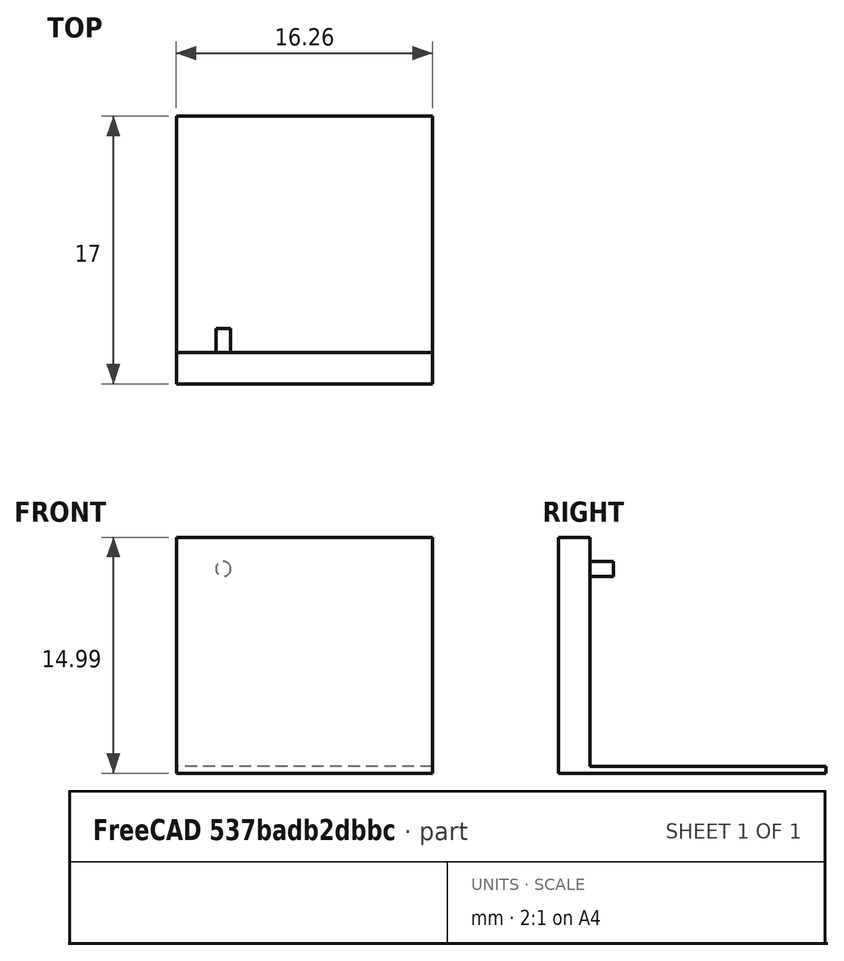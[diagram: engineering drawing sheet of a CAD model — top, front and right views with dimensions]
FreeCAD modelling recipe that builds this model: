
FCSTD DOCUMENT  (FreeCAD 0.20R29603 (Git))
Label: base
License: All rights reserved
LicenseURL: http://en.wikipedia.org/wiki/All_rights_reserved
objects: Mesh::Feature×5, Sketcher::SketchObject×3, PartDesign::Pad×3, PartDesign::Plane×1, PartDesign::Line×1, PartDesign::Point×1, PartDesign::Body×1
note: 13 computed .brp shape members not serialized (recipe doc carries the construction recipe); baked Part::Feature solids carry a one-line shape summary decoded from their .brp

FEATURE [Mesh::Feature] sla
FEATURE [Mesh::Feature] ps
FEATURE [Mesh::Feature] i_sclerite
FEATURE [Mesh::Feature] pwp
FEATURE [Mesh::Feature] ii_sclerite
FEATURE [PartDesign::Plane] DatumPlane  label="sidewall_DatumPlane"
  AttachmentOffset = pos=(0,0,6) rot=(0,0,1;0rad)
  Length = 60
  MapMode = 5
  Placement = pos=(0,-6,1.3e-15) rot=(1,0,0;1.5708rad)
  ResizeMode = 0
  Support = -> [XZ_Plane]
  Width = 60
FEATURE [Sketcher::SketchObject] Sketch  label="sidewall_Sketch"
  FullyConstrained = true
  MapMode = 5
  Placement = pos=(0,-6,1.3e-15) rot=(1,0,0;1.5708rad)
  Support = -> [DatumPlane]
  sketch-geometry (4):
    g0: LineSegment StartX=-12.0172 StartY=14.9884 StartZ=0 EndX=4.2382 EndY=14.9884 EndZ=0
    g1: LineSegment StartX=4.2382 StartY=14.9884 StartZ=0 EndX=4.2382 EndY=0 EndZ=0
    g2: LineSegment StartX=4.2382 StartY=0 StartZ=0 EndX=-12.0172 EndY=0 EndZ=0
    g3: LineSegment StartX=-12.0172 StartY=0 StartZ=0 EndX=-12.0172 EndY=14.9884 EndZ=0
  constraints (12):
    c: Coincident(g0,g1)
    c: Coincident(g1,g2)
    c: Coincident(g2,g3)
    c: Coincident(g3,g0)
    c: Horizontal(g0)
    c: Horizontal(g2)
    c: Vertical(g1)
    c: Vertical(g3)
    c: PointOnObject(g1,g-1)
    c: Distance(g1) = 14.9884
    c: Distance(g2) = 16.2554
    c: Distance(g-1,g1) = 4.2382
FEATURE [PartDesign::Pad] Pad  label="sidewall_Pad"
  Direction = (0,-1,2e-16)
  Length = 2
  Length2 = 10
  Placement = pos=(0,-6,1.3e-15) rot=(1,0,0;1.5708rad)
  Profile = -> Sketch
  ReferenceAxis = -> Sketch [N_Axis]
  Type = 0
FEATURE [Sketcher::SketchObject] Sketch001
  ExternalGeometry = -> [Pad]
  FullyConstrained = true
  MapMode = 5
  Placement = pos=(0,-6,1.3e-15) rot=(-1,0,0;1.5708rad)
  Support = -> [Pad]
  sketch-geometry (4):
    g0: LineSegment StartX=4.2382 StartY=-0.455 StartZ=0 EndX=-12.0172 EndY=-0.455 EndZ=0
    g1: LineSegment StartX=-12.0172 StartY=-0.455 StartZ=0 EndX=-12.0172 EndY=0 EndZ=0
    g2: LineSegment StartX=-12.0172 StartY=0 StartZ=0 EndX=4.2382 EndY=0 EndZ=0
    g3: LineSegment StartX=4.2382 StartY=0 StartZ=0 EndX=4.2382 EndY=-0.455 EndZ=0
  constraints (10):
    c: Coincident(g0,g1)
    c: Coincident(g1,g2)
    c: Coincident(g2,g3)
    c: Coincident(g3,g0)
    c: Horizontal(g0)
    c: Vertical(g1)
    c: Vertical(g3)
    c: Coincident(g1,g-3)
    c: Coincident(g-4,g2)
    c: DistanceY(g3,g3) = 0.455
FEATURE [PartDesign::Pad] Pad001  label="floorpad_Pad"
  BaseFeature = -> Pad
  Direction = (0,1,-2e-16)
  Length = 15
  Length2 = 10
  Placement = pos=(0,-6,1.3e-15) rot=(1,0,0;1.5708rad)
  Profile = -> Sketch001
  ReferenceAxis = -> Sketch001 [N_Axis]
  Type = 0
FEATURE [Sketcher::SketchObject] Sketch002  label="sla_axis_Sketch"
  FullyConstrained = true
  MapMode = 5
  Placement = pos=(0,-6,1.3e-15) rot=(0,0.707107,0.707107;3.14159rad)
  Support = -> [DatumPlane]
  sketch-geometry (1):
    g0: Circle CenterX=9.03232 CenterY=12.985 CenterZ=0 NormalX=0 NormalY=0 NormalZ=1 AngleXU=0 Radius=0.4711
  constraints (3):
    c: DistanceX(g0) = 9.03232
    c: DistanceY(g0) = 12.985
    c: Diameter(g0) = 0.9422
FEATURE [PartDesign::Pad] Pad002  label="sla_axis_Pad"
  BaseFeature = -> Pad001
  Direction = (0,1,-2e-16)
  Length = 1.5
  Length2 = 10
  Placement = pos=(0,-6,1.3e-15) rot=(1,0,0;1.5708rad)
  Profile = -> Sketch002
  ReferenceAxis = -> Sketch002 [N_Axis]
  Type = 0
FEATURE [PartDesign::Line] DatumLine  label="sla_axis_DatumLine"
  AttacherType = Attacher::AttachEngineLine
  Length = 20
  MapMode = 19
  Placement = pos=(-9.03232,-4.5,12.985) rot=(0,0.707107,0.707107;3.14159rad)
  ResizeMode = 0
  Support = -> [Pad002]
FEATURE [PartDesign::Point] DatumPoint  label="sla_axis_DatumPoint"
  AttacherType = Attacher::AttachEnginePoint
  MapMode = 36
  Placement = pos=(-9.03232,-4.5,12.985) rot=(0,1,0;3.14159rad)
  Support = -> [Pad002]
FEATURE [PartDesign::Body] Body  label="base_Body"
  Group = -> [DatumPlane,Sketch,Pad,Sketch001,Pad001,Sketch002,Pad002,DatumLine,DatumPoint]
  Origin = -> Origin
  Tip = -> Pad002
